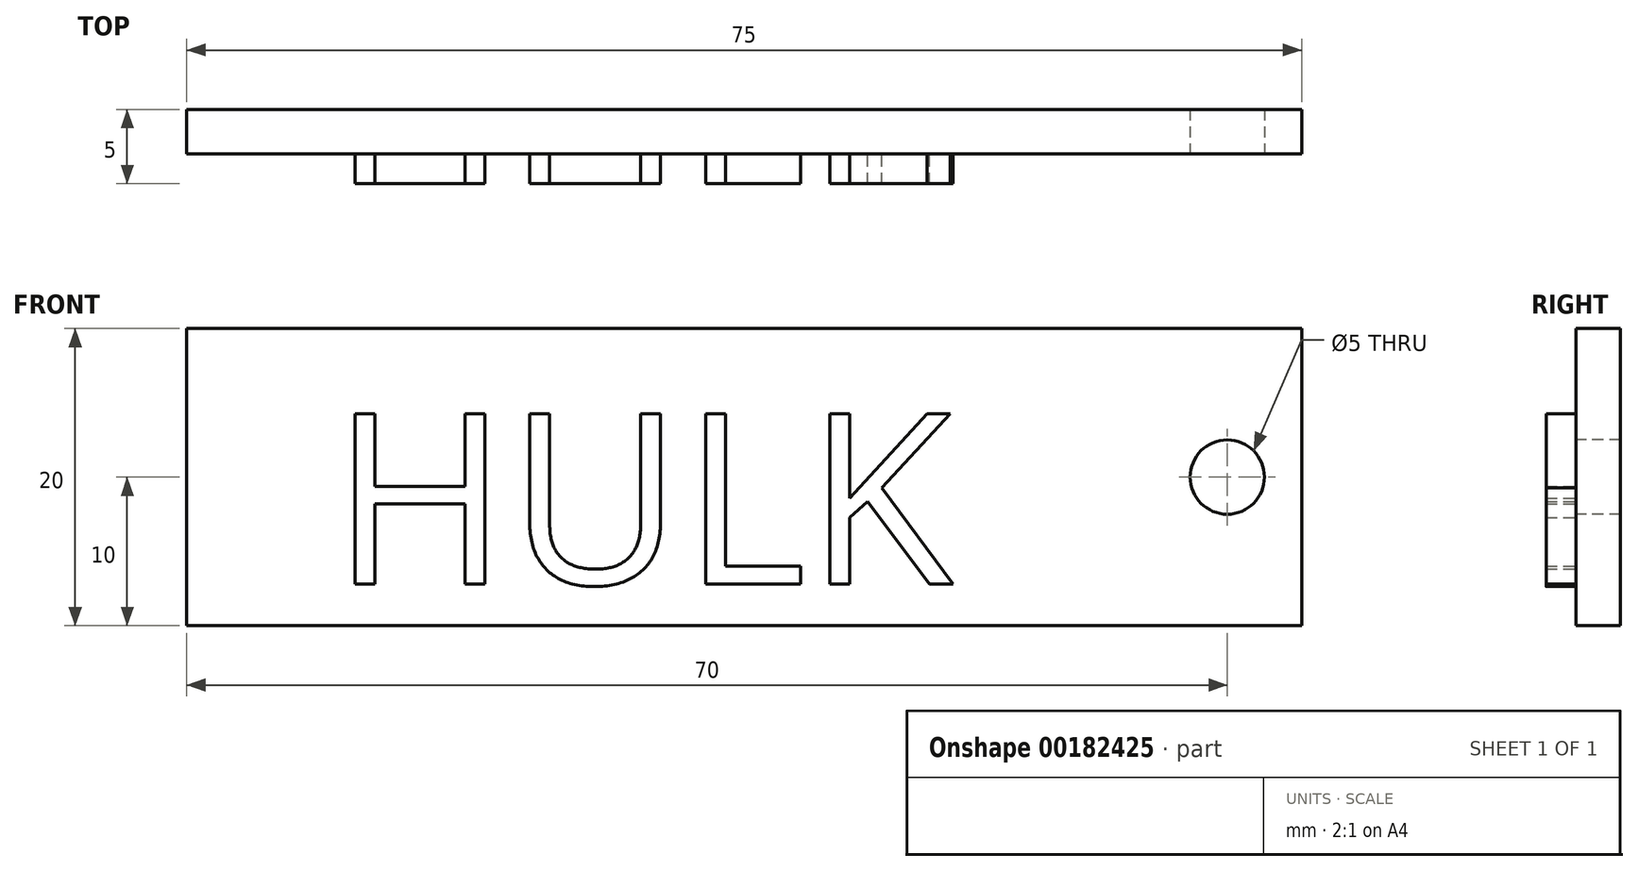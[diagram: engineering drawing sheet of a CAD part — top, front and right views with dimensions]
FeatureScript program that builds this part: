
annotation { "Feature Type Name" : "Feature", "Feature Type Description" : "" }
export const myFeature = defineFeature(function(context is Context, id is Id, definition is map)
    precondition{}
    {
        {
            var Q0;
            Q0=qCreatedBy(makeId("Front.planeOp"),FACE);
            var sketch = newSketch(context, id + "F0", { "sketchPlane" : qUnion([Q0])});
            skLineSegment(sketch, "E0.bottom", {"start": v(0, 0) * mm, "end": v(75, 0) * mm});
            skLineSegment(sketch, "E0.top", {"start": v(0, -20) * mm, "end": v(75, -20) * mm});
            skLineSegment(sketch, "E0.left", {"start": v(0, 0) * mm, "end": v(0, -20) * mm});
            skLineSegment(sketch, "E0.right", {"start": v(75, 0) * mm, "end": v(75, -20) * mm});
            skCircle(sketch, "E1", {"center": v(70, -10) * mm, "radius": 2.5 * mm});
            skSolve(sketch);
        }
        {
            var Q0;
            Q0 = qSketchRegion(id + "F0", true);
            extrude(context, id + "F1", {"entities" : qUnion([Q0]), "oppositeDirection" : true, "depth" : 3 * mm});
        }
        {
            var Q0;
            Q0=makeQuery(id+"F1.opExtrude","CAP_FACE",FACE,{"disambiguationData":[OSD([sQuery(id+"F0.wireOp",EDGE,"E0.bottom"),sQuery(id+"F0.wireOp",EDGE,"E0.top"),sQuery(id+"F0.wireOp",EDGE,"E0.left"),sQuery(id+"F0.wireOp",EDGE,"E0.right"),sQuery(id+"F0.wireOp",EDGE,"E1")])],"isStart":true});
            var sketch = newSketch(context, id + "F2", { "sketchPlane" : qUnion([Q0])});
            skText(sketch, "E2", { "text": "HULK", "fontName": "OpenSans-Regular.ttf"});
            const initialGuessF2  = {"E2": [0.00975, -0.01721, 1, 0, 0.01158]};
            skSetInitialGuess(sketch, initialGuessF2);
            skSolve(sketch);
        }
        {
            var Q0;
            Q0 = qSketchRegion(id + "F2", true);
            extrude(context, id + "F3", {"entities" : qUnion([Q0]), "operationType" : NewBodyOperationType.ADD, "depth" : 2 * mm});
        }
    });
